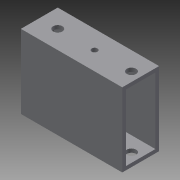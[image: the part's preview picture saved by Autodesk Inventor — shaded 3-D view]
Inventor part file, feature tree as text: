
AUTODESK INVENTOR PART (.ipt)
format: ipt  version: 2015 SP1 (Build 190203100, 203)  size: 125,952 bytes
history: native  units: in
note: dims shown in document units (in); Inventor stores cm internally (conversion verified against a paired STEP export)
features: sketch x4, projected_geometry x3, extrude x2, hole x2
ambient origin geometry x8: Origin, YZ Plane, XZ Plane, XY Plane, X Axis, Y Axis, Z Axis, Center Point
bodies: Solid1 (feature_tree)
feature tree (11):
  extrude  "Extrusion1"  Depth=1.0in
  hole  "Hole1"  [1 undecoded]
  extrude  "Extrusion2"  Depth=0.1in
  hole  "Hole2"  [1 undecoded]
  sketch  "Sketch1"  dims[d0=2.0in d1=1.0in]
  sketch  "Sketch2"  dims[d2=1.8in d3=0.8in]
  projected_geometry  "Projected Loop1"
  sketch  "Sketch3"  dims[d4=0.1in d5=0.1in]
  projected_geometry  "Projected Loop2"
  sketch  "Sketch4"  dims[d6=2.75in d7=0.0in d8=0.5in d9=0.5in d10=0.5in d11=0.5in d12=1.5in d13=2.5in d14=0.1562in d15=0.75in d16=0.375in d17=0.25in d18=0.5635in d19=1.0in d20=0.8108in d21=0.25in d22=0.25in d23=2.75in d24=0.0in d25=0.5in d26=1.5in d27=0.3125in d28=0.75in d29=0.375in d30=0.25in d31=0.5635in d32=1.0in d33=0.8108in]
  projected_geometry  "Projected Loop3"
note: 2 required parameter values undecoded (feature->parameter linkage not recoverable at this tier; creation-order binding heuristic only, values carry confidence <= 0.55)
